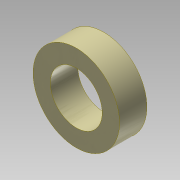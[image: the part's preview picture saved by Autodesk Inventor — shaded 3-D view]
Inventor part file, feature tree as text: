
AUTODESK INVENTOR PART (.ipt)
format: ipt  version: 2013 SP2 (Build 170200200, 200)  size: 81,920 bytes
history: native  units: mm
features: extrude x1, sketch x1
ambient origin geometry x8: Origin, YZ Plane, XZ Plane, XY Plane, X Axis, Y Axis, Z Axis, Center Point
bodies: Solid1 (feature_tree)
feature tree (2):
  extrude  "Extrusion1"  Depth=2.0mm
  sketch  "Sketch1"  dims[d0=6.0mm d2=2.0mm d3=3.175mm d4=0.0mm]
